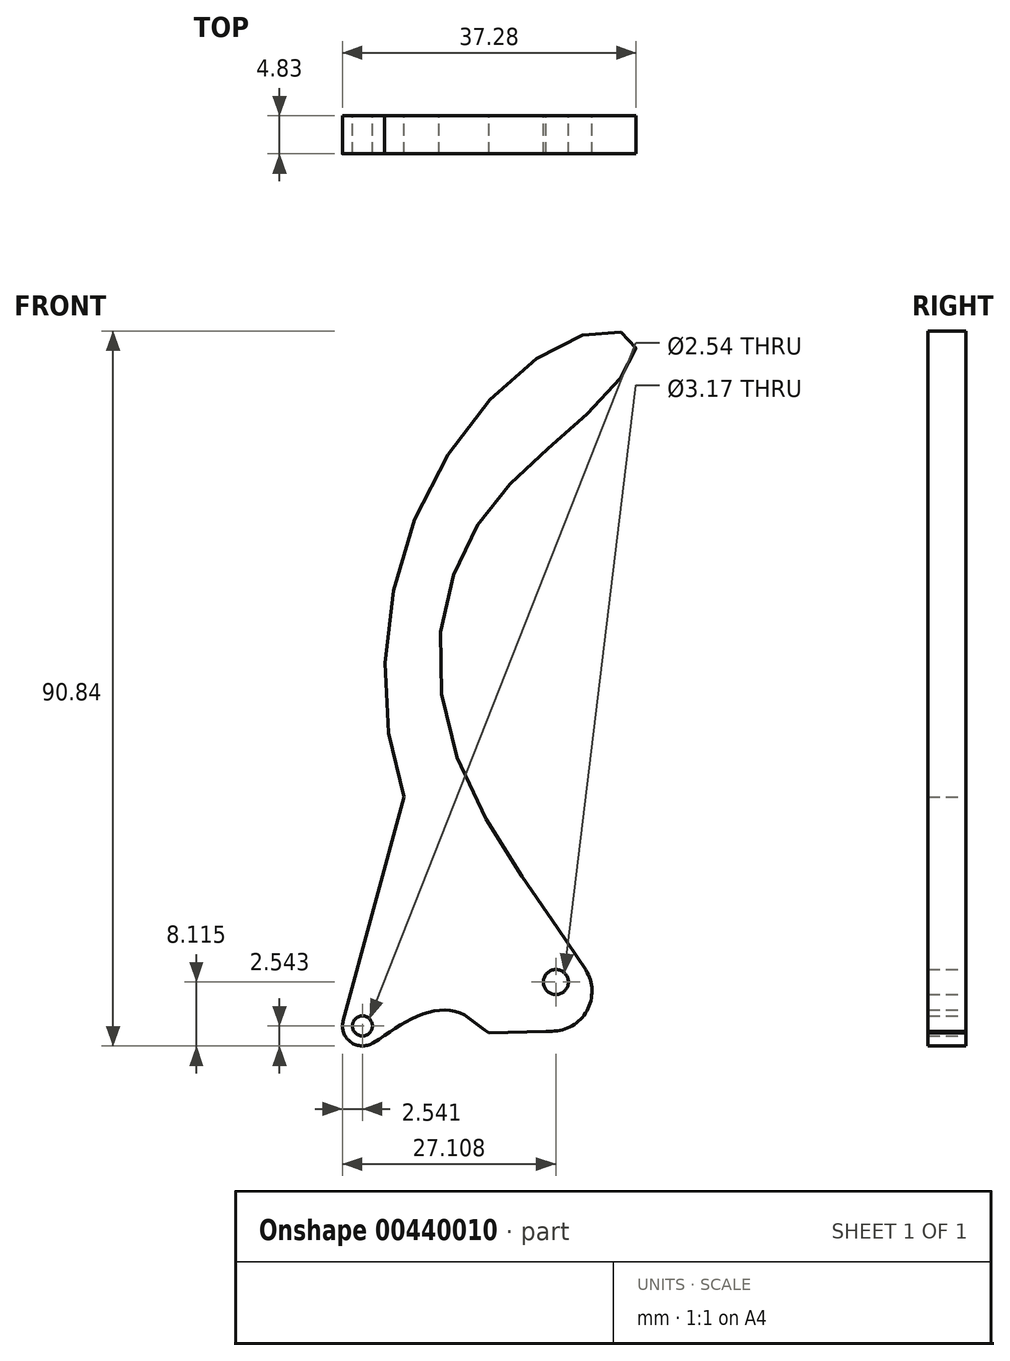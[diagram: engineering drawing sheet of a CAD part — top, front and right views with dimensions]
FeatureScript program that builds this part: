
annotation { "Feature Type Name" : "Feature", "Feature Type Description" : "" }
export const myFeature = defineFeature(function(context is Context, id is Id, definition is map)
    precondition{}
    {
        {
            var Q0;
            Q0=qCreatedBy(makeId("Front.planeOp"),FACE);
            var sketch = newSketch(context, id + "F0", { "sketchPlane" : qUnion([Q0])});
            skLineSegment(sketch, "E0", {"start": v(8.95, -26.08) * mm, "end": v(16.17, -25.9) * mm});
            skCircle(sketch, "E1", {"center": v(-7.1, -25.22) * mm, "radius": 1.27 * mm});
            skCircle(sketch, "E2", {"center": v(-7.1, -25.22) * mm, "radius": 2.54 * mm});
            skLineSegment(sketch, "E3", {"start": v(-9.56, -24.55) * mm, "end": v(-1.86, 3.88) * mm});
            skFitSpline(sketch, "E4", {"points": [v(-5.74, -27.36) * mm, v(0.4, -23.76) * mm, v(5.32, -23.57) * mm, v(8.95, -26.08) * mm], "startDerivative": vector(16.29, 10.4) * mm, "endDerivative": vector(13.23, -7.1) * mm});
            skLineSegment(sketch, "E5", {"start": v(10.27, -15.4) * mm, "end": v(10.27, -15.4) * mm});
            skLineSegment(sketch, "E6", {"start": v(10.28, -15.4) * mm, "end": v(10.27, -15.4) * mm});
            skLineSegment(sketch, "E7", {"start": v(9.41, -13.5) * mm, "end": v(9.35, -13.37) * mm});
            skFitSpline(sketch, "E8", {"points": [v(16.17, -25.9) * mm, v(10.28, -15.4) * mm, v(-1.86, 3.88) * mm, v(0, 40.25) * mm, v(20.14, 62.33) * mm, v(27.54, 61.63) * mm, v(21.17, 52.32) * mm, v(6.98, 37.6) * mm, v(3.92, 11.9) * mm, v(19.51, -15.4) * mm, v(25.6, -25.9) * mm], "startDerivative": vector(-62.7, 129.59) * mm, "endDerivative": vector(61.14, -118.55) * mm});
            skLineSegment(sketch, "E9", {"start": v(16.17, -25.9) * mm, "end": v(25.6, -25.9) * mm});
            skCircle(sketch, "E10", {"center": v(17.46, -19.64) * mm, "radius": 1.59 * mm});
            skSolve(sketch);
        }
        {
            var Q0;
            {var subQ3=sQuery(id+"F0.wireOp",EDGE,"E0");Q0=makeQuery(id+"F0.imprint","IMPRINT",FACE,{"disambiguationData":[TD([[makeQuery(id+"F0.imprint","IMPRINT",EDGE,{"derivedFrom":subQ3}),1.0]])]});}
            var Q1;
            Q1=makeQuery(id+"F0.imprint","IMPRINT",FACE,{"disambiguationData":[TD([[makeQuery(id+"F0.imprint","IMPRINT",EDGE,{"derivedFrom":sQuery(id+"F0.wireOp",EDGE,"E1")}),-1.0]])]});
            var Q2;
            {var subQ0=sQuery(id+"F0.wireOp",EDGE,"E9");Q2=makeQuery(id+"F0.imprint","IMPRINT",FACE,{"disambiguationData":[TD([[makeQuery(id+"F0.imprint","IMPRINT",EDGE,{"derivedFrom":subQ0}),1.0]])]});}
            extrude(context, id + "F1", {"entities" : qUnion([Q0, Q1, Q2]), "depth" : 4.83 * mm});
        }
        {
            var Q0;
            Q0=makeQuery(id+"F1.opExtrude","SWEPT_EDGE",EDGE,{"disambiguationData":[OSD([sQuery(id+"F0.wireOp",EDGE,"E8"),sQuery(id+"F0.wireOp",EDGE,"E9")])]});
            fillet(context, id + "F2", {"entities" : qUnion([Q0]), "radius" : 5.08 * mm, "tangentPropagation" : true, "allowEdgeOverflow" : false});
        }
    });
